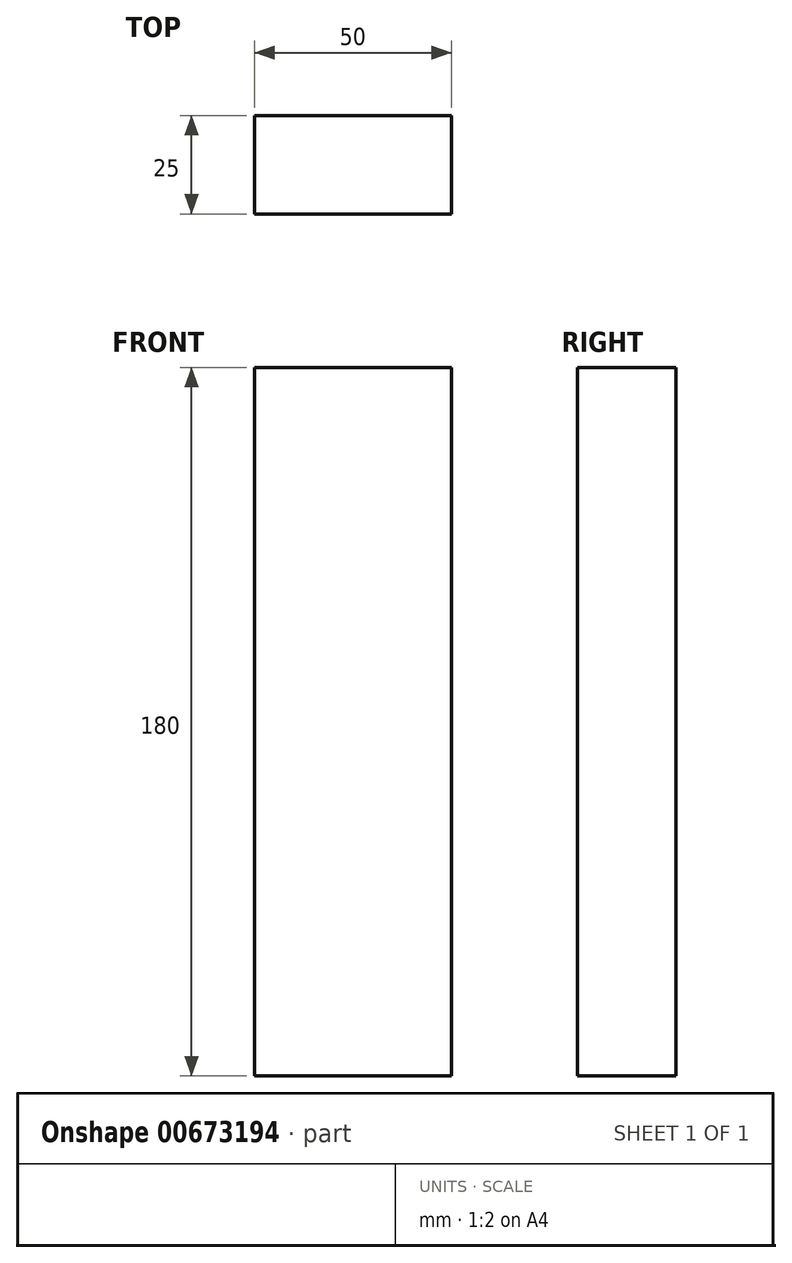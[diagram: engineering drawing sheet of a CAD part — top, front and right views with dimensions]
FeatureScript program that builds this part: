
annotation { "Feature Type Name" : "Feature", "Feature Type Description" : "" }
export const myFeature = defineFeature(function(context is Context, id is Id, definition is map)
    precondition{}
    {
        {
            var Q0;
            Q0=qCreatedBy(makeId("Front.planeOp"),FACE);
            var sketch = newSketch(context, id + "F0", { "sketchPlane" : qUnion([Q0])});
            skLineSegment(sketch, "E0.bottom", {"start": v(0, 0) * mm, "end": v(50, 0) * mm});
            skLineSegment(sketch, "E0.top", {"start": v(0, 180) * mm, "end": v(50, 180) * mm});
            skLineSegment(sketch, "E0.left", {"start": v(0, 0) * mm, "end": v(0, 180) * mm});
            skLineSegment(sketch, "E0.right", {"start": v(50, 0) * mm, "end": v(50, 180) * mm});
            skSolve(sketch);
        }
        {
            var Q0;
            Q0=qSketchRegion(id+"F0",true);
            extrude(context, id + "F1", {"entities" : qUnion([Q0]), "depth" : 25 * mm});
        }
    });
